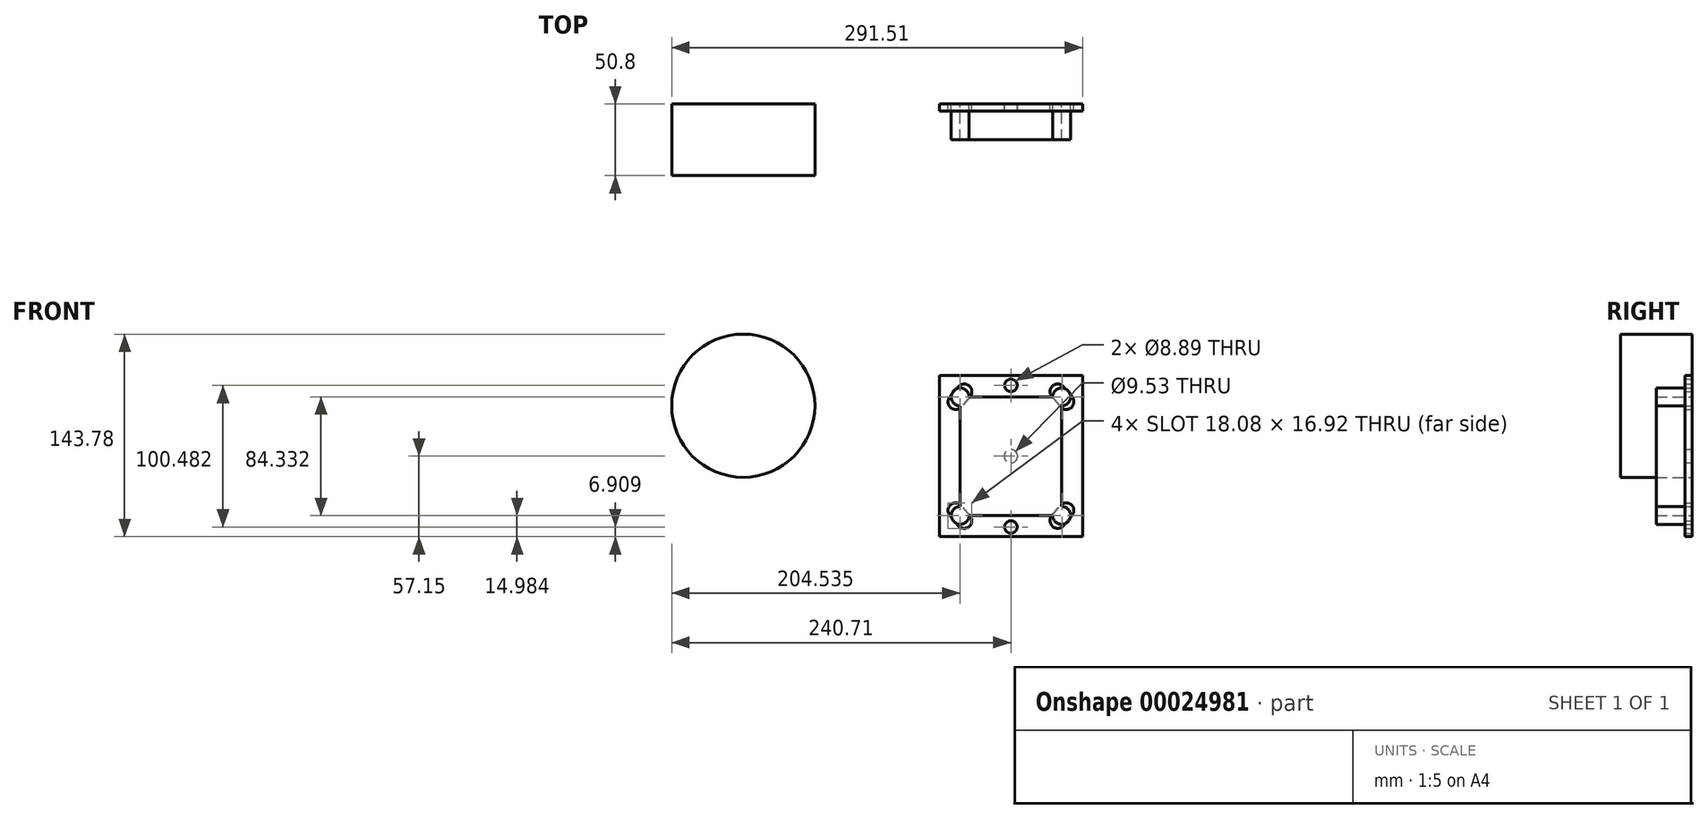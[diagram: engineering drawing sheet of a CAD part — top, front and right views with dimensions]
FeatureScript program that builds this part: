
annotation { "Feature Type Name" : "Feature", "Feature Type Description" : "" }
export const myFeature = defineFeature(function(context is Context, id is Id, definition is map)
    precondition{}
    {
        {
            var Q0;
            Q0=qCreatedBy(makeId("Front.planeOp"),FACE);
            var sketch = newSketch(context, id + "F0", { "sketchPlane" : qUnion([Q0])});
            skLineSegment(sketch, "E0.bottom", {"start": v(-50.8, 57.15) * mm, "end": v(50.8, 57.15) * mm});
            skLineSegment(sketch, "E0.top", {"start": v(-50.8, -57.15) * mm, "end": v(50.8, -57.15) * mm});
            skLineSegment(sketch, "E0.left", {"start": v(-50.8, 57.15) * mm, "end": v(-50.8, -57.15) * mm});
            skLineSegment(sketch, "E0.right", {"start": v(50.8, 57.15) * mm, "end": v(50.8, -57.15) * mm});
            skCircle(sketch, "E1", {"center": v(0, 50.24) * mm, "radius": 4.45 * mm});
            skLineSegment(sketch, "E2.bottom", {"start": v(-37.34, 49.28) * mm, "end": v(-26.42, 49.28) * mm});
            skLineSegment(sketch, "E2.top", {"start": v(-37.34, 39.88) * mm, "end": v(-26.42, 39.88) * mm});
            skLineSegment(sketch, "E2.left", {"start": v(-37.34, 49.28) * mm, "end": v(-37.34, 39.88) * mm});
            skLineSegment(sketch, "E2.right", {"start": v(-26.42, 49.28) * mm, "end": v(-26.42, 39.88) * mm});
            skArc(sketch, "E3", {"start": v(-37.34, 49.28) * mm, "mid": v(-31.88, 54.74) * mm, "end": v(-26.42, 49.28) * mm});
            skArc(sketch, "E4", {"start": v(-37.34, 39.88) * mm, "mid": v(-31.88, 34.42) * mm, "end": v(-26.42, 39.88) * mm});
            skCircle(sketch, "E5.MirrorC", {"center": v(0, -50.24) * mm, "radius": 4.45 * mm});
            skCircle(sketch, "E6", {"center": v(0, 0) * mm, "radius": 4.76 * mm});
            skLineSegment(sketch, "E7", {"start": v(0, 38.1) * mm, "end": v(0, -38.1) * mm});
            skSolve(sketch);
        }
        {
            var Q0;
            Q0=makeQuery(id+"F0.imprint","IMPRINT",FACE,{"disambiguationData":[TD([[makeQuery(id+"F0.imprint","IMPRINT",EDGE,{"derivedFrom":sQuery(id+"F0.wireOp",EDGE,"E0.bottom")}),-1.0]])]});
            var Q1;
            Q1=makeQuery(id+"F0.imprint","IMPRINT",FACE,{"disambiguationData":[TD([[makeQuery(id+"F0.imprint","IMPRINT",EDGE,{"derivedFrom":sQuery(id+"F0.wireOp",EDGE,"E2.top")}),-1.0]])]});
            var Q2;
            Q2=makeQuery(id+"F0.imprint","IMPRINT",FACE,{"disambiguationData":[TD([[makeQuery(id+"F0.imprint","IMPRINT",EDGE,{"derivedFrom":sQuery(id+"F0.wireOp",EDGE,"E2.bottom")}),-1.0]])]});
            var Q3;
            Q3=makeQuery(id+"F0.imprint","IMPRINT",FACE,{"disambiguationData":[TD([[makeQuery(id+"F0.imprint","IMPRINT",EDGE,{"derivedFrom":sQuery(id+"F0.wireOp",EDGE,"E2.bottom")}),1.0]])]});
            extrude(context, id + "F1", {"entities" : qUnion([Q0, Q1, Q2, Q3]), "depth" : 5.08 * mm});
        }
        {
            var Q0;
            Q0=makeQuery(id+"F0.imprint","IMPRINT",FACE,{"disambiguationData":[TD([[makeQuery(id+"F0.imprint","IMPRINT",EDGE,{"derivedFrom":sQuery(id+"F0.wireOp",EDGE,"E2.bottom")}),-1.0]])]});
            var Q1;
            Q1=makeQuery(id+"F0.imprint","IMPRINT",FACE,{"disambiguationData":[TD([[makeQuery(id+"F0.imprint","IMPRINT",EDGE,{"derivedFrom":sQuery(id+"F0.wireOp",EDGE,"E2.top")}),-1.0]])]});
            var Q2;
            Q2=makeQuery(id+"F0.imprint","IMPRINT",FACE,{"disambiguationData":[TD([[makeQuery(id+"F0.imprint","IMPRINT",EDGE,{"derivedFrom":sQuery(id+"F0.wireOp",EDGE,"E2.bottom")}),1.0]])]});
            extrude(context, id + "F2", {"entities" : qUnion([Q0, Q1, Q2]), "depth" : 5.08 * mm});
        }
        {
            var Q0;
            Q0=makeQuery(id+"F2.opExtrude","SWEPT_BODY",BODY,{"disambiguationData":[OSD([sQuery(id+"F0.wireOp",EDGE,"E2.left"),sQuery(id+"F0.wireOp",EDGE,"E2.right"),sQuery(id+"F0.wireOp",EDGE,"E3"),sQuery(id+"F0.wireOp",EDGE,"E4")])]});
            var Q1;
            Q1=makeQuery(id+"F2.opExtrude","SWEPT_EDGE",EDGE,{"disambiguationData":[OSD([sQuery(id+"F0.wireOp",EDGE,"E2.bottom"),sQuery(id+"F0.wireOp",EDGE,"E2.left"),sQuery(id+"F0.wireOp",EDGE,"E3")])]});
            transform(context, id + "F3", {"entities" : qUnion([Q0]), "transformType" : TransformType.ROTATION, "transformAxis" : qUnion([Q1]), "angle" : 40 * degree, "makeCopy" : false});
        }
        {
            var Q0;
            Q0=makeQuery(id+"F2.opExtrude","SWEPT_BODY",BODY,{"disambiguationData":[OSD([sQuery(id+"F0.wireOp",EDGE,"E2.left"),sQuery(id+"F0.wireOp",EDGE,"E2.right"),sQuery(id+"F0.wireOp",EDGE,"E3"),sQuery(id+"F0.wireOp",EDGE,"E4")])]});
            var Q1;
            Q1=qCreatedBy(makeId("Right.planeOp"),FACE);
            mirror(context, id + "F4", {"entities" : qUnion([Q0]), "mirrorPlane" : qUnion([Q1])});
        }
        {
            var Q0;
            Q0=makeQuery(id+"F2.opExtrude","SWEPT_BODY",BODY,{"disambiguationData":[OSD([sQuery(id+"F0.wireOp",EDGE,"E2.left"),sQuery(id+"F0.wireOp",EDGE,"E2.right"),sQuery(id+"F0.wireOp",EDGE,"E3"),sQuery(id+"F0.wireOp",EDGE,"E4")])]});
            var Q1;
            Q1=makeQuery(id+"F4.opPattern","COPY",BODY,{"derivedFrom":makeQuery(id+"F2.opExtrude","SWEPT_BODY",BODY,{"disambiguationData":[OSD([sQuery(id+"F0.wireOp",EDGE,"E2.left"),sQuery(id+"F0.wireOp",EDGE,"E2.right"),sQuery(id+"F0.wireOp",EDGE,"E3"),sQuery(id+"F0.wireOp",EDGE,"E4")])]}),"instanceName":"1"});
            var Q2;
            Q2=qCreatedBy(makeId("Top.planeOp"),FACE);
            mirror(context, id + "F5", {"entities" : qUnion([Q0, Q1]), "mirrorPlane" : qUnion([Q2])});
        }
        {
            var Q0;
            Q0=makeQuery(id+"F2.opExtrude","SWEPT_BODY",BODY,{"disambiguationData":[OSD([sQuery(id+"F0.wireOp",EDGE,"E2.left"),sQuery(id+"F0.wireOp",EDGE,"E2.right"),sQuery(id+"F0.wireOp",EDGE,"E3"),sQuery(id+"F0.wireOp",EDGE,"E4")])]});
            var Q1;
            Q1=makeQuery(id+"F4.opPattern","COPY",BODY,{"derivedFrom":makeQuery(id+"F2.opExtrude","SWEPT_BODY",BODY,{"disambiguationData":[OSD([sQuery(id+"F0.wireOp",EDGE,"E2.left"),sQuery(id+"F0.wireOp",EDGE,"E2.right"),sQuery(id+"F0.wireOp",EDGE,"E3"),sQuery(id+"F0.wireOp",EDGE,"E4")])]}),"instanceName":"1"});
            var Q2;
            Q2=makeQuery(id+"F5.opPattern","COPY",BODY,{"derivedFrom":makeQuery(id+"F4.opPattern","COPY",BODY,{"derivedFrom":makeQuery(id+"F2.opExtrude","SWEPT_BODY",BODY,{"disambiguationData":[OSD([sQuery(id+"F0.wireOp",EDGE,"E2.left"),sQuery(id+"F0.wireOp",EDGE,"E2.right"),sQuery(id+"F0.wireOp",EDGE,"E3"),sQuery(id+"F0.wireOp",EDGE,"E4")])]}),"instanceName":"1"}),"instanceName":"1"});
            var Q3;
            Q3=makeQuery(id+"F5.opPattern","COPY",BODY,{"derivedFrom":makeQuery(id+"F2.opExtrude","SWEPT_BODY",BODY,{"disambiguationData":[OSD([sQuery(id+"F0.wireOp",EDGE,"E2.left"),sQuery(id+"F0.wireOp",EDGE,"E2.right"),sQuery(id+"F0.wireOp",EDGE,"E3"),sQuery(id+"F0.wireOp",EDGE,"E4")])]}),"instanceName":"1"});
            var Q4;
            Q4=makeQuery(id+"F1.opExtrude","SWEPT_BODY",BODY,{"disambiguationData":[OSD([sQuery(id+"F0.wireOp",EDGE,"E0.bottom"),sQuery(id+"F0.wireOp",EDGE,"E0.top"),sQuery(id+"F0.wireOp",EDGE,"E0.left"),sQuery(id+"F0.wireOp",EDGE,"E0.right"),sQuery(id+"F0.wireOp",EDGE,"E1"),sQuery(id+"F0.wireOp",EDGE,"E5.MirrorC")])]});
            booleanBodies(context, id + "F6", {"operationType" : BooleanOperationType.SUBTRACTION, "tools" : qUnion([Q0, Q1, Q2, Q3]), "targets" : qUnion([Q4]), "keepTools" : true});
        }
        {
            var Q0;
            Q0=qCreatedBy(makeId("Front.planeOp"),FACE);
            var sketch = newSketch(context, id + "F7", { "sketchPlane" : qUnion([Q0])});
            skCircle(sketch, "E8", {"center": v(-189.91, 35.83) * mm, "radius": 50.8 * mm});
            skSolve(sketch);
        }
        {
            var Q0;
            Q0 = qSketchRegion(id + "F7", true);
            extrude(context, id + "F8", {"entities" : qUnion([Q0]), "depth" : 50.8 * mm});
        }
        {
            var Q0;
            Q0=qCreatedBy(makeId("Front.planeOp"),FACE);
            var sketch = newSketch(context, id + "F9", { "sketchPlane" : qUnion([Q0])});
            skLineSegment(sketch, "E9.bottom", {"start": v(-36, 42) * mm, "end": v(36, 42) * mm});
            skLineSegment(sketch, "E9.top", {"start": v(-36, -42) * mm, "end": v(36, -42) * mm});
            skLineSegment(sketch, "E9.left", {"start": v(-36, 42) * mm, "end": v(-36, -42) * mm});
            skLineSegment(sketch, "E9.right", {"start": v(36, 42) * mm, "end": v(36, -42) * mm});
            skLineSegment(sketch, "E10", {"start": v(0, 42) * mm, "end": v(0, -42) * mm});
            skPoint(sketch, "E11", {"position": v(0, 0) * mm});
            skCircle(sketch, "E12", {"center": v(36, -42) * mm, "radius": 6.35 * mm});
            skCircle(sketch, "E13", {"center": v(-36, 42) * mm, "radius": 6.35 * mm});
            skCircle(sketch, "E14", {"center": v(36, 42) * mm, "radius": 6.35 * mm});
            skCircle(sketch, "E15", {"center": v(-36, -42) * mm, "radius": 6.35 * mm});
            skSolve(sketch);
        }
        {
            var Q0;
            {var subQ0=sQuery(id+"F9.wireOp",EDGE,"E9.left");var subQ1=sQuery(id+"F9.wireOp",EDGE,"E9.bottom");var subQ2=makeQuery(id+"F9.imprint","INTERSECT",VERTEX,{"derivedFrom":[subQ1,subQ0]});Q0=makeQuery(id+"F9.imprint","IMPRINT",FACE,{"disambiguationData":[TD([[makeQuery(id+"F9.imprint","IMPRINT",EDGE,{"disambiguationData":[TD([[subQ2,-1.0]])],"derivedFrom":subQ1}),1.0]])]});}
            var Q1;
            {var subQ0=sQuery(id+"F9.wireOp",EDGE,"E9.right");var subQ1=sQuery(id+"F9.wireOp",EDGE,"E9.bottom");var subQ2=makeQuery(id+"F9.imprint","INTERSECT",VERTEX,{"derivedFrom":[subQ1,subQ0]});Q1=makeQuery(id+"F9.imprint","IMPRINT",FACE,{"disambiguationData":[TD([[makeQuery(id+"F9.imprint","IMPRINT",EDGE,{"disambiguationData":[TD([[subQ2,1.0]])],"derivedFrom":subQ1}),1.0]])]});}
            var Q2;
            {var subQ0=sQuery(id+"F9.wireOp",EDGE,"E9.right");var subQ1=sQuery(id+"F9.wireOp",EDGE,"E9.top");var subQ2=makeQuery(id+"F9.imprint","INTERSECT",VERTEX,{"derivedFrom":[subQ1,subQ0]});Q2=makeQuery(id+"F9.imprint","IMPRINT",FACE,{"disambiguationData":[TD([[makeQuery(id+"F9.imprint","IMPRINT",EDGE,{"disambiguationData":[TD([[subQ2,1.0]])],"derivedFrom":subQ1}),-1.0]])]});}
            var Q3;
            {var subQ0=sQuery(id+"F9.wireOp",EDGE,"E9.left");var subQ1=sQuery(id+"F9.wireOp",EDGE,"E9.top");var subQ2=makeQuery(id+"F9.imprint","INTERSECT",VERTEX,{"derivedFrom":[subQ1,subQ0]});Q3=makeQuery(id+"F9.imprint","IMPRINT",FACE,{"disambiguationData":[TD([[makeQuery(id+"F9.imprint","IMPRINT",EDGE,{"disambiguationData":[TD([[subQ2,-1.0]])],"derivedFrom":subQ1}),-1.0]])]});}
            var Q4;
            {var subQ0=sQuery(id+"F9.wireOp",EDGE,"E10");Q4=makeQuery(id+"F9.imprint","IMPRINT",FACE,{"disambiguationData":[TD([[makeQuery(id+"F9.imprint","IMPRINT",EDGE,{"derivedFrom":subQ0}),-1.0]])]});}
            var Q5;
            {var subQ0=sQuery(id+"F9.wireOp",EDGE,"E10");Q5=makeQuery(id+"F9.imprint","IMPRINT",FACE,{"disambiguationData":[TD([[makeQuery(id+"F9.imprint","IMPRINT",EDGE,{"derivedFrom":subQ0}),1.0]])]});}
            var Q6;
            {var subQ0=sQuery(id+"F9.wireOp",EDGE,"E9.left");var subQ1=sQuery(id+"F9.wireOp",EDGE,"E9.top");var subQ2=makeQuery(id+"F9.imprint","INTERSECT",VERTEX,{"derivedFrom":[subQ1,subQ0]});Q6=makeQuery(id+"F9.imprint","IMPRINT",FACE,{"disambiguationData":[TD([[makeQuery(id+"F9.imprint","IMPRINT",EDGE,{"disambiguationData":[TD([[subQ2,-1.0]])],"derivedFrom":subQ1}),1.0]])]});}
            var Q7;
            {var subQ0=sQuery(id+"F9.wireOp",EDGE,"E9.right");var subQ1=sQuery(id+"F9.wireOp",EDGE,"E9.top");var subQ2=makeQuery(id+"F9.imprint","INTERSECT",VERTEX,{"derivedFrom":[subQ1,subQ0]});Q7=makeQuery(id+"F9.imprint","IMPRINT",FACE,{"disambiguationData":[TD([[makeQuery(id+"F9.imprint","IMPRINT",EDGE,{"disambiguationData":[TD([[subQ2,1.0]])],"derivedFrom":subQ1}),1.0]])]});}
            var Q8;
            {var subQ0=sQuery(id+"F9.wireOp",EDGE,"E9.right");var subQ1=sQuery(id+"F9.wireOp",EDGE,"E9.bottom");var subQ2=makeQuery(id+"F9.imprint","INTERSECT",VERTEX,{"derivedFrom":[subQ1,subQ0]});Q8=makeQuery(id+"F9.imprint","IMPRINT",FACE,{"disambiguationData":[TD([[makeQuery(id+"F9.imprint","IMPRINT",EDGE,{"disambiguationData":[TD([[subQ2,1.0]])],"derivedFrom":subQ1}),-1.0]])]});}
            var Q9;
            {var subQ0=sQuery(id+"F9.wireOp",EDGE,"E9.left");var subQ1=sQuery(id+"F9.wireOp",EDGE,"E9.bottom");var subQ2=makeQuery(id+"F9.imprint","INTERSECT",VERTEX,{"derivedFrom":[subQ1,subQ0]});Q9=makeQuery(id+"F9.imprint","IMPRINT",FACE,{"disambiguationData":[TD([[makeQuery(id+"F9.imprint","IMPRINT",EDGE,{"disambiguationData":[TD([[subQ2,-1.0]])],"derivedFrom":subQ1}),-1.0]])]});}
            extrude(context, id + "F10", {"entities" : qUnion([Q0, Q1, Q2, Q3, Q4, Q5, Q6, Q7, Q8, Q9]), "depth" : 25.4 * mm});
        }
    });
